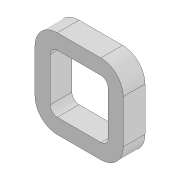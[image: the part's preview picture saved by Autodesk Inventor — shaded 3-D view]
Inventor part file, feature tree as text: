
AUTODESK INVENTOR PART (.ipt)
format: ipt  version: 2020 (Build 240168000, 168)  size: 104,448 bytes
history: native  units: mm
features: other x7, extrude x1, sketch x1
ambient origin geometry x8: Origin, YZ Plane, XZ Plane, XY Plane, X Axis, Y Axis, Z Axis, Center Point
bodies: Body1 (feature_tree)
feature tree (9):
  other  "Sólido1"
  other  "Plano de trabalho1"
  extrude  "Extrusão1"  [1 undecoded]
  sketch  "Esboço1"  dims[d0=30.0mm d1=0.0mm]
  other  "Referência1"
  other  "<userpath>\OneDrive\Área de Trabalho\Calorimetro 2022\Inventor\parte_superior.iam"
  other  "parte_superior.iam"
  other  "Corpo_1:4"
  other  "Base_isolante:1"
note: 1 required parameter value undecoded (feature->parameter linkage not recoverable at this tier; creation-order binding heuristic only, values carry confidence <= 0.55)
